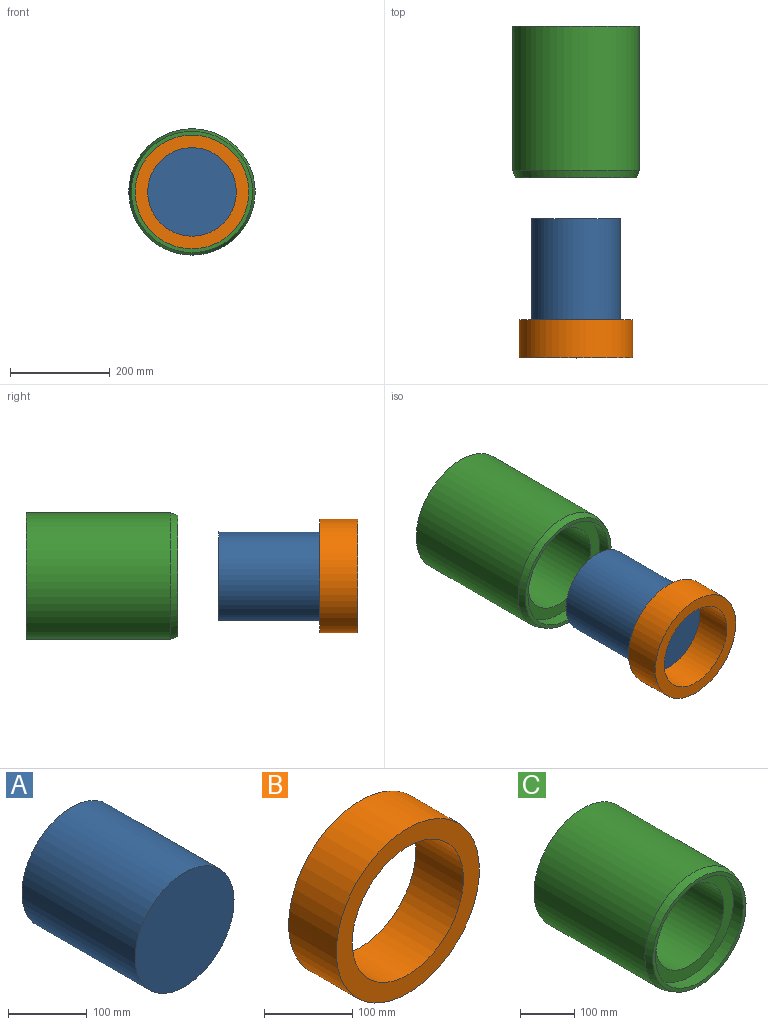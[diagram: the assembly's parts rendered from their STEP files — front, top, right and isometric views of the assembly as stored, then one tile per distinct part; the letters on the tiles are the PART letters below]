
ASSEMBLY  parts=3 mates=2
PART A: 3 faces, bbox 177.8x203.2x177.8 mm
  f0: cylinder r=88.9mm len=203.2mm, axis (0,1,0), area 113502.5mm2, adj f1,f2
  f1: plane 177.8x177.8mm, normal (0,-1,0), area 24828.7mm2, adj f0
  f2: plane 177.8x177.8mm, normal (0,1,0), area 24828.7mm2, adj f0
PART B: 4 faces, bbox 228.6x76.2x228.6 mm
  f0: cylinder r=88.9mm len=177.8mm, axis (0,1,0), area 42563.4mm2, adj f2,f3
  f1: cylinder r=114.3mm len=228.6mm, axis (0,1,0), area 54724.4mm2, adj f2,f3
  f2: plane 228.6x228.6mm, normal (0,-1,0), area 16214.6mm2, adj f0,f1
  f3: plane 228.6x228.6mm, normal (0,1,0), area 16214.6mm2, adj f0,f1
PART C: 8 faces, bbox 254x304.8x254 mm
  f0: cylinder r=127mm len=289.56mm, axis (0,1,0), area 231058.6mm2, adj f2,f3
  f1: plane 243.84x243.84mm, normal (0,-1,0), area 5654.9mm2, adj f3,f6
  f2: plane 254x254mm, normal (0,1,0), area 50670.7mm2, adj f0
  f3: cone r=121.92mm half-angle=18.4deg, axis (0,1,0), area 12562.4mm2, adj f0,f1
  f4: cylinder r=88.9mm len=177.8mm, axis (0,-1,0), area 99314.7mm2, adj f5,f7
  f5: plane 228.6x228.6mm, normal (0,-1,0), area 16214.6mm2, adj f4,f6
  f6: cylinder r=114.3mm len=228.6mm, axis (0,-1,0), area 18241.5mm2, adj f1,f5
  f7: cone r=0mm half-angle=59deg, axis (0,-1,0), area 28966mm2, adj f4
PLACE A t=(140.92,-451.8,-133.51)mm
PLACE B t=(140.92,-451.8,-133.51)mm
PLACE C t=(408.19,-64.34,-11.79)mm
MATE slider A.f0 <-> C.f0  axis (0,1,0) through (408.19,-451.8,-577.04)mm
MATE cylindrical C.f0 <-> B.f0  axis (0,1,0) through (408.19,-209.12,-577.04)mm
